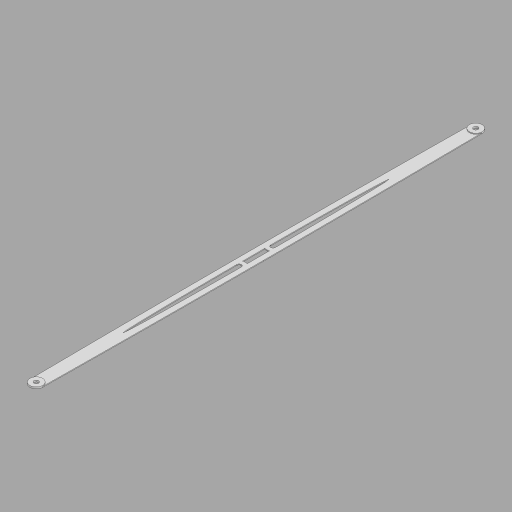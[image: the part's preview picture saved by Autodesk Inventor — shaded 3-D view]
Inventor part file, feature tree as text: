
AUTODESK INVENTOR PART (.ipt)
format: ipt  version: 2023 (Build 270158000, 158)  size: 134,656 bytes
history: native  units: mm
features: extrude x3, sketch x1
ambient origin geometry x8: Origin, YZ Plane, XZ Plane, XY Plane, X Axis, Y Axis, Z Axis, Center Point
bodies: Solid1 (feature_tree)
feature tree (4):
  sketch  "Sketch1"  dims[d0=244.423mm d1=90.0deg d2=41.005864mm d3=244.423mm d4=5.5mm d5=5.5mm d6=5.5mm d7=15.0mm d8=15.0mm d9=18.0mm d10=5.5mm d11=2.0mm d12=0.0mm d13=1.0mm d14=0.0mm d15=160.0mm d16=15.0mm d17=15.0mm d18=1.0mm d19=0.0mm]
  extrude  "Extrusion1"  TaperAngle=90.0deg  [1 undecoded]
  extrude  "Extrusion2"  Depth=1.0mm
  extrude  "Extrusion3"  Depth=244.423mm
note: 1 required parameter value undecoded (feature->parameter linkage not recoverable at this tier; creation-order binding heuristic only, values carry confidence <= 0.55)
